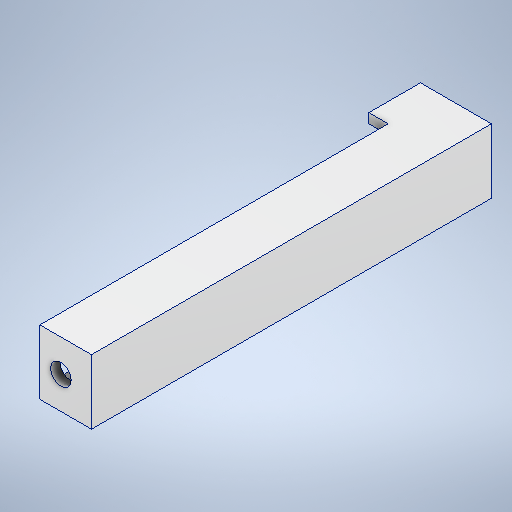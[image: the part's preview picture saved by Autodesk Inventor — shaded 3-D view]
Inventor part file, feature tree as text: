
AUTODESK INVENTOR PART (.ipt)
format: ipt  version: 2025 (Build 290162000, 162)  size: 300,032 bytes
history: native  units: mm
features: sketch x7, projected_geometry x5, extrude x4, hole x3, other x1
ambient origin geometry x8: Origin, YZ Plane, XZ Plane, XY Plane, X Axis, Y Axis, Z Axis, Center Point
bodies: Body1 (feature_tree)
feature tree (20):
  other  "Těleso1"
  extrude  "Vysunutí1"  Depth=8.0mm
  extrude  "Vysunutí2"  Depth=10.0mm
  hole  "Díra1"  [1 undecoded]
  extrude  "Vysunutí3"  Depth=7.0mm
  extrude  "Vysunutí4"  Depth=1.5mm
  hole  "Díra3"  [1 undecoded]
  hole  "Díra4"  [1 undecoded]
  sketch  "Náčrt1"
  sketch  "Náčrt2"
  projected_geometry  "Promítnutá smyčka1"
  sketch  "Náčrt3"
  projected_geometry  "Promítnutá smyčka2"
  sketch  "Náčrt5"
  sketch  "Náčrt6"
  projected_geometry  "Promítnutá smyčka4"
  sketch  "Náčrt7"
  projected_geometry  "Promítnutá smyčka5"
  sketch  "Náčrt8"
  projected_geometry  "Promítnutá smyčka6"
note: 3 required parameter values undecoded (feature->parameter linkage not recoverable at this tier; creation-order binding heuristic only, values carry confidence <= 0.55)
